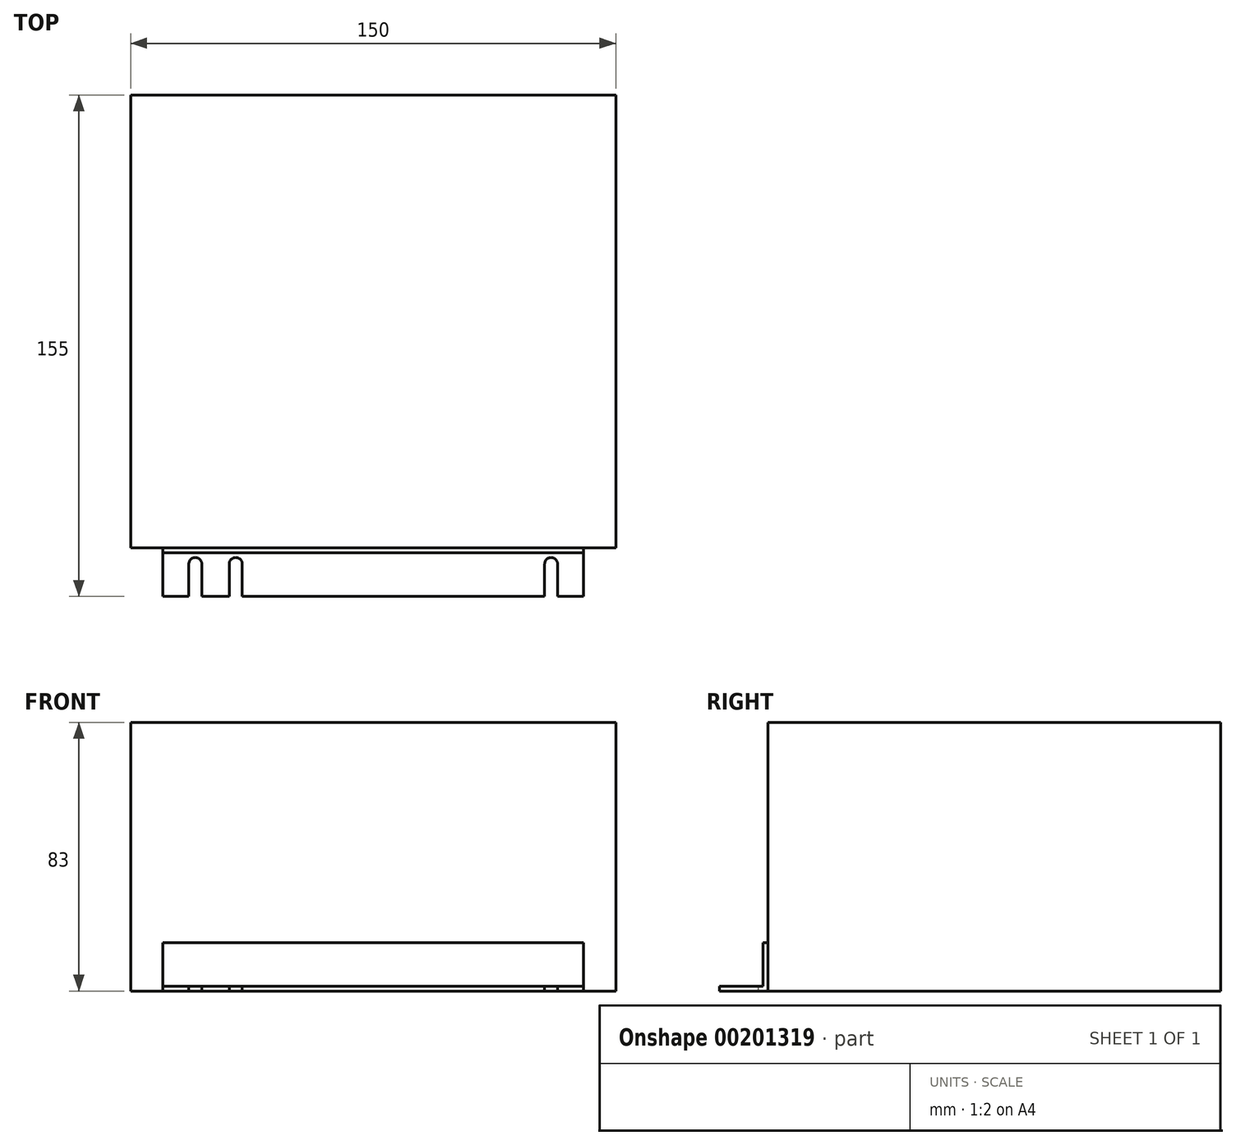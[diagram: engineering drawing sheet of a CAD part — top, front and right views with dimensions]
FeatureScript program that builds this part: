
annotation { "Feature Type Name" : "Feature", "Feature Type Description" : "" }
export const myFeature = defineFeature(function(context is Context, id is Id, definition is map)
    precondition{}
    {
        {
            var Q0;
            Q0=qCreatedBy(makeId("Top.planeOp"),FACE);
            var sketch = newSketch(context, id + "F0", { "sketchPlane" : qUnion([Q0])});
            skLineSegment(sketch, "E0.bottom", {"start": v(75, 70) * mm, "end": v(-75, 70) * mm});
            skLineSegment(sketch, "E0.top", {"start": v(75, -70) * mm, "end": v(-75, -70) * mm});
            skLineSegment(sketch, "E0.left", {"start": v(75, -70) * mm, "end": v(75, 70) * mm});
            skLineSegment(sketch, "E0.right", {"start": v(-75, 70) * mm, "end": v(-75, -70) * mm});
            skPoint(sketch, "E0.middle", {"position": v(0, 0) * mm});
            skPoint(sketch, "E1.middle", {"position": v(75, 70) * mm});
            skLineSegment(sketch, "E2", {"start": v(-65, -85) * mm, "end": v(65, -85) * mm});
            skLineSegment(sketch, "E3", {"start": v(65, -85) * mm, "end": v(65, -70) * mm});
            skLineSegment(sketch, "E4", {"start": v(-65, -85) * mm, "end": v(-65, -70) * mm});
            skLineSegment(sketch, "E5", {"start": v(-55, -92.81) * mm, "end": v(-55, -57.41) * mm, "construction": true});
            skCircle(sketch, "E6", {"center": v(-55, -75) * mm, "radius": 2 * mm});
            skLineSegment(sketch, "E7", {"start": v(-57, -85) * mm, "end": v(-57, -75) * mm});
            skLineSegment(sketch, "E8", {"start": v(-53, -85) * mm, "end": v(-53, -75) * mm});
            skLineSegment(sketch, "E9.1.0.0", {"start": v(-40.5, -85) * mm, "end": v(-40.5, -75) * mm});
            skLineSegment(sketch, "E9.1.0.1", {"start": v(-44.5, -85) * mm, "end": v(-44.5, -75) * mm});
            skCircle(sketch, "E9.1.0.2", {"center": v(-42.5, -75) * mm, "radius": 2 * mm});
            skLineSegment(sketch, "E9.direction1", {"start": v(-57, -85) * mm, "end": v(-44.5, -85) * mm, "construction": true});
            skLineSegment(sketch, "E10.1.0.0", {"start": v(53, -85) * mm, "end": v(53, -75) * mm});
            skLineSegment(sketch, "E10.1.0.1", {"start": v(57, -85) * mm, "end": v(57, -75) * mm});
            skCircle(sketch, "E10.1.0.2", {"center": v(55, -75) * mm, "radius": 2 * mm});
            skLineSegment(sketch, "E10.direction1", {"start": v(-57, -85) * mm, "end": v(53, -85) * mm, "construction": true});
            skLineSegment(sketch, "E11", {"start": v(-65, -71.5) * mm, "end": v(65, -71.5) * mm});
            skSolve(sketch);
        }
        {
            var Q0;
            Q0=makeQuery(id+"F0.imprint","IMPRINT",FACE,{"disambiguationData":[TD([[makeQuery(id+"F0.imprint","IMPRINT",EDGE,{"derivedFrom":sQuery(id+"F0.wireOp",EDGE,"E0.bottom")}),1.0]])]});
            extrude(context, id + "F1", {"entities" : qUnion([Q0]), "depth" : 83 * mm});
        }
        {
            var Q0;
            {var subQ8=sQuery(id+"F0.wireOp",EDGE,"E3");Q0=makeQuery(id+"F0.imprint","IMPRINT",FACE,{"disambiguationData":[TD([[makeQuery(id+"F0.imprint","IMPRINT",EDGE,{"derivedFrom":subQ8}),1.0]])]});}
            var Q1;
            {var subQ5=sQuery(id+"F0.wireOp",EDGE,"E7");Q1=makeQuery(id+"F0.imprint","IMPRINT",FACE,{"disambiguationData":[TD([[makeQuery(id+"F0.imprint","IMPRINT",EDGE,{"derivedFrom":subQ5}),1.0]])]});}
            extrude(context, id + "F2", {"entities" : qUnion([Q0, Q1]), "operationType" : NewBodyOperationType.ADD, "depth" : 1.5 * mm});
        }
        {
            var Q0;
            {var subQ5=sQuery(id+"F0.wireOp",EDGE,"E11");Q0=makeQuery(id+"F0.imprint","IMPRINT",FACE,{"disambiguationData":[TD([[makeQuery(id+"F0.imprint","IMPRINT",EDGE,{"derivedFrom":subQ5}),1.0]])]});}
            extrude(context, id + "F3", {"entities" : qUnion([Q0]), "operationType" : NewBodyOperationType.ADD, "depth" : 15 * mm});
        }
    });
